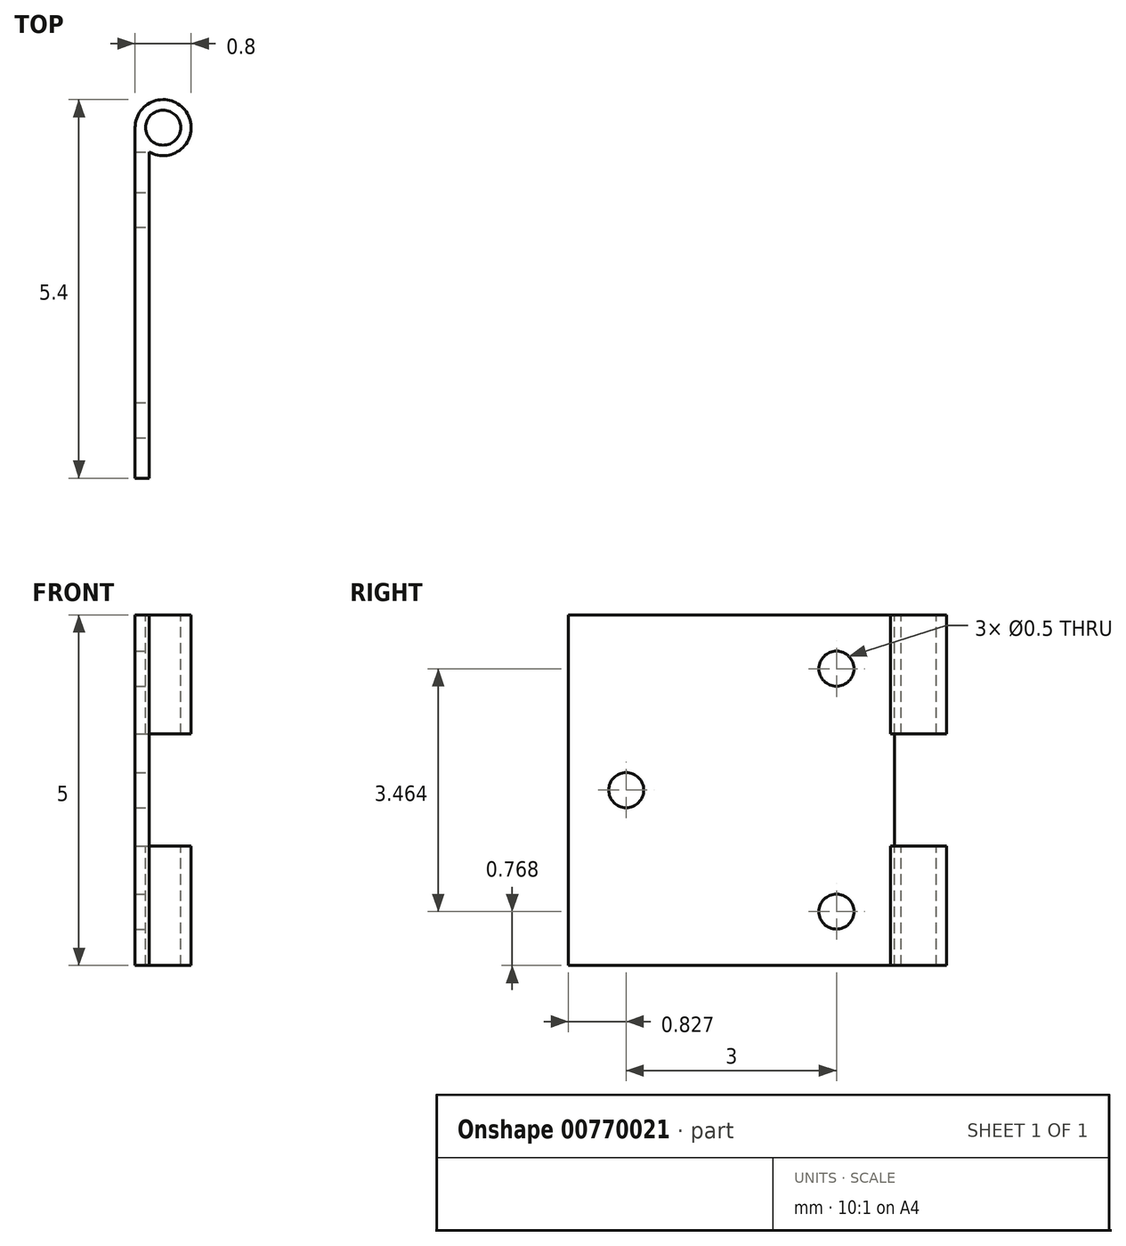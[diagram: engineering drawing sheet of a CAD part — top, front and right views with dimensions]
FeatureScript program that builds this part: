
annotation { "Feature Type Name" : "Feature", "Feature Type Description" : "" }
export const myFeature = defineFeature(function(context is Context, id is Id, definition is map)
    precondition{}
    {
        {
            var Q0;
            Q0=qCreatedBy(makeId("Front.planeOp"),FACE);
            var sketch = newSketch(context, id + "F0", { "sketchPlane" : qUnion([Q0])});
            skLineSegment(sketch, "E0", {"start": v(0, 0) * mm, "end": v(0, -5) * mm});
            skLineSegment(sketch, "E1", {"start": v(0, -5) * mm, "end": v(0.2, -5) * mm});
            skLineSegment(sketch, "E2", {"start": v(0.2, -5) * mm, "end": v(0.2, 0) * mm});
            skLineSegment(sketch, "E3", {"start": v(0.2, 0) * mm, "end": v(0, 0) * mm});
            skSolve(sketch);
        }
        {
            var Q0;
            Q0 = qSketchRegion(id + "F0", true);
            extrude(context, id + "F1", {"entities" : qUnion([Q0]), "oppositeDirection" : true, "depth" : 5 * mm, "offsetDistance" : 25 * mm});
        }
        {
            var Q0;
            Q0=makeQuery(id+"F1.opExtrude","SWEPT_FACE",FACE,{"disambiguationData":[OSD([sQuery(id+"F0.wireOp",EDGE,"E3")])]});
            var sketch = newSketch(context, id + "F2", { "sketchPlane" : qUnion([Q0])});
            skCircle(sketch, "E4", {"center": v(0.4, 5) * mm, "radius": 0.4 * mm});
            skSolve(sketch);
        }
        {
            var Q0;
            Q0 = qSketchRegion(id + "F2", true);
            extrude(context, id + "F3", {"entities" : qUnion([Q0]), "operationType" : NewBodyOperationType.ADD, "oppositeDirection" : true, "depth" : 5 * mm, "offsetDistance" : 25 * mm});
        }
        {
            var Q0;
            Q0=makeQuery(id+"F3.boolean.opBoolean","MERGE",FACE,{"derivedFrom":[makeQuery(id+"F1.opExtrude","SWEPT_FACE",FACE,{"disambiguationData":[OSD([sQuery(id+"F0.wireOp",EDGE,"E3")])]}),makeQuery(id+"F3.opExtrude","CAP_FACE",FACE,{"disambiguationData":[OSD([sQuery(id+"F2.wireOp",EDGE,"E4")])],"isStart":true})]});
            var sketch = newSketch(context, id + "F4", { "sketchPlane" : qUnion([Q0])});
            skCircle(sketch, "E5", {"center": v(0.4, 5) * mm, "radius": 0.25 * mm});
            skSolve(sketch);
        }
        {
            var Q0;
            Q0 = qSketchRegion(id + "F4", true);
            extrude(context, id + "F5", {"entities" : qUnion([Q0]), "operationType" : NewBodyOperationType.REMOVE, "endBound" : BoundingType.THROUGH_ALL, "oppositeDirection" : true, "depth" : 25 * mm, "offsetDistance" : 25 * mm});
        }
        {
            var Q0;
            Q0=makeQuery(id+"F1.opExtrude","CAP_FACE",FACE,{"disambiguationData":[OSD([sQuery(id+"F0.wireOp",EDGE,"E0"),sQuery(id+"F0.wireOp",EDGE,"E1"),sQuery(id+"F0.wireOp",EDGE,"E2"),sQuery(id+"F0.wireOp",EDGE,"E3")])],"isStart":true});
            var sketch = newSketch(context, id + "F6", { "sketchPlane" : qUnion([Q0])});
            skLineSegment(sketch, "E6", {"start": v(0.2, -2.5) * mm, "end": v(0.93, -2.5) * mm});
            skLineSegment(sketch, "E7", {"start": v(0.2, -2.5) * mm, "end": v(0.2, -1.7) * mm});
            skLineSegment(sketch, "E8", {"start": v(0.2, -2.5) * mm, "end": v(0.2, -3.3) * mm});
            skLineSegment(sketch, "E9", {"start": v(0.2, -1.7) * mm, "end": v(0.93, -1.7) * mm});
            skLineSegment(sketch, "E10", {"start": v(0.93, -1.7) * mm, "end": v(0.93, -2.5) * mm});
            skLineSegment(sketch, "E11", {"start": v(0.2, -3.3) * mm, "end": v(0.93, -3.3) * mm});
            skLineSegment(sketch, "E12", {"start": v(0.93, -3.3) * mm, "end": v(0.93, -2.5) * mm});
            skSolve(sketch);
        }
        {
            var Q0;
            Q0 = qSketchRegion(id + "F6", true);
            extrude(context, id + "F7", {"entities" : qUnion([Q0]), "operationType" : NewBodyOperationType.REMOVE, "endBound" : BoundingType.THROUGH_ALL, "oppositeDirection" : true, "depth" : 25 * mm, "offsetDistance" : 25 * mm});
        }
        {
            var Q0;
            Q0=makeQuery(id+"F7.boolean.opBoolean","MERGE",FACE,{"derivedFrom":[makeQuery(id+"F1.opExtrude","SWEPT_FACE",FACE,{"disambiguationData":[OSD([sQuery(id+"F0.wireOp",EDGE,"E2")])]}),makeQuery(id+"F7.opExtrude","SWEPT_FACE",FACE,{"disambiguationData":[OSD([sQuery(id+"F6.wireOp",EDGE,"E7"),sQuery(id+"F6.wireOp",EDGE,"E8")])]})]});
            var sketch = newSketch(context, id + "F8", { "sketchPlane" : qUnion([Q0])});
            skLineSegment(sketch, "E13", {"start": v(4.65, -1.7) * mm, "end": v(4.65, -3.3) * mm});
            skLineSegment(sketch, "E14", {"start": v(4.65, -3.3) * mm, "end": v(5.7, -3.3) * mm});
            skLineSegment(sketch, "E15", {"start": v(5.7, -3.3) * mm, "end": v(5.7, -1.7) * mm});
            skLineSegment(sketch, "E16", {"start": v(5.7, -1.7) * mm, "end": v(4.65, -1.7) * mm});
            skSolve(sketch);
        }
        {
            var Q0;
            Q0 = qSketchRegion(id + "F8", true);
            extrude(context, id + "F9", {"entities" : qUnion([Q0]), "operationType" : NewBodyOperationType.REMOVE, "endBound" : BoundingType.THROUGH_ALL, "oppositeDirection" : true, "depth" : 25 * mm, "offsetDistance" : 25 * mm});
        }
        {
            var Q0;
            Q0=makeQuery(id+"F7.boolean.opBoolean","MERGE",FACE,{"derivedFrom":[makeQuery(id+"F1.opExtrude","SWEPT_FACE",FACE,{"disambiguationData":[OSD([sQuery(id+"F0.wireOp",EDGE,"E2")])]}),makeQuery(id+"F7.opExtrude","SWEPT_FACE",FACE,{"disambiguationData":[OSD([sQuery(id+"F6.wireOp",EDGE,"E7"),sQuery(id+"F6.wireOp",EDGE,"E8")])]})]});
            var sketch = newSketch(context, id + "F10", { "sketchPlane" : qUnion([Q0])});
            skLineSegment(sketch, "E17", {"start": v(2.33, -2.5) * mm, "end": v(2.83, -2.5) * mm});
            skPoint(sketch, "E17.startSnap0", {"position": v(4.65, -2.5) * mm});
            skPoint(sketch, "E17.startSnap1", {"position": v(2.33, -5) * mm});
            skCircle(sketch, "E18.cCircle", {"center": v(2.83, -2.5) * mm, "radius": 1 * mm, "construction": true});
            skLineSegment(sketch, "E18.0", {"start": v(3.83, -0.77) * mm, "end": v(3.83, -4.23) * mm});
            skLineSegment(sketch, "E18.1", {"start": v(3.83, -4.23) * mm, "end": v(0.83, -2.5) * mm});
            skLineSegment(sketch, "E18.2", {"start": v(0.83, -2.5) * mm, "end": v(3.83, -0.77) * mm});
            skPoint(sketch, "E18.0.midPoint", {"position": v(3.83, -2.5) * mm});
            skCircle(sketch, "E19", {"center": v(3.83, -4.23) * mm, "radius": 0.25 * mm});
            skCircle(sketch, "E20", {"center": v(0.83, -2.5) * mm, "radius": 0.25 * mm});
            skCircle(sketch, "E21", {"center": v(3.83, -0.77) * mm, "radius": 0.25 * mm});
            skSolve(sketch);
        }
        {
            var Q0;
            {var subQ0=sQuery(id+"F10.wireOp",EDGE,"E18.2");var subQ1=sQuery(id+"F10.wireOp",EDGE,"E18.0");var subQ2=makeQuery(id+"F10.imprint","INTERSECT",VERTEX,{"derivedFrom":[subQ1,subQ0]});Q0=makeQuery(id+"F10.imprint","IMPRINT",FACE,{"disambiguationData":[TD([[makeQuery(id+"F10.imprint","IMPRINT",EDGE,{"disambiguationData":[TD([[subQ2,-1.0]])],"derivedFrom":subQ1}),-1.0]])]});}
            var Q1;
            {var subQ0=sQuery(id+"F10.wireOp",EDGE,"E18.2");var subQ1=sQuery(id+"F10.wireOp",EDGE,"E18.0");var subQ2=makeQuery(id+"F10.imprint","INTERSECT",VERTEX,{"derivedFrom":[subQ1,subQ0]});Q1=makeQuery(id+"F10.imprint","IMPRINT",FACE,{"disambiguationData":[TD([[makeQuery(id+"F10.imprint","IMPRINT",EDGE,{"disambiguationData":[TD([[subQ2,-1.0]])],"derivedFrom":subQ1}),1.0]])]});}
            var Q2;
            {var subQ0=sQuery(id+"F10.wireOp",EDGE,"E18.1");var subQ1=sQuery(id+"F10.wireOp",EDGE,"E18.0");var subQ2=makeQuery(id+"F10.imprint","INTERSECT",VERTEX,{"derivedFrom":[subQ1,subQ0]});Q2=makeQuery(id+"F10.imprint","IMPRINT",FACE,{"disambiguationData":[TD([[makeQuery(id+"F10.imprint","IMPRINT",EDGE,{"disambiguationData":[TD([[subQ2,1.0]])],"derivedFrom":subQ1}),-1.0]])]});}
            var Q3;
            {var subQ0=sQuery(id+"F10.wireOp",EDGE,"E18.1");var subQ1=sQuery(id+"F10.wireOp",EDGE,"E18.0");var subQ2=makeQuery(id+"F10.imprint","INTERSECT",VERTEX,{"derivedFrom":[subQ1,subQ0]});Q3=makeQuery(id+"F10.imprint","IMPRINT",FACE,{"disambiguationData":[TD([[makeQuery(id+"F10.imprint","IMPRINT",EDGE,{"disambiguationData":[TD([[subQ2,1.0]])],"derivedFrom":subQ1}),1.0]])]});}
            var Q4;
            {var subQ0=sQuery(id+"F10.wireOp",EDGE,"E18.2");var subQ1=sQuery(id+"F10.wireOp",EDGE,"E18.1");var subQ2=makeQuery(id+"F10.imprint","INTERSECT",VERTEX,{"derivedFrom":[subQ1,subQ0]});Q4=makeQuery(id+"F10.imprint","IMPRINT",FACE,{"disambiguationData":[TD([[makeQuery(id+"F10.imprint","IMPRINT",EDGE,{"disambiguationData":[TD([[subQ2,1.0]])],"derivedFrom":subQ1}),1.0]])]});}
            var Q5;
            {var subQ0=sQuery(id+"F10.wireOp",EDGE,"E18.2");var subQ1=sQuery(id+"F10.wireOp",EDGE,"E18.1");var subQ2=makeQuery(id+"F10.imprint","INTERSECT",VERTEX,{"derivedFrom":[subQ1,subQ0]});Q5=makeQuery(id+"F10.imprint","IMPRINT",FACE,{"disambiguationData":[TD([[makeQuery(id+"F10.imprint","IMPRINT",EDGE,{"disambiguationData":[TD([[subQ2,1.0]])],"derivedFrom":subQ1}),-1.0]])]});}
            extrude(context, id + "F11", {"entities" : qUnion([Q0, Q1, Q2, Q3, Q4, Q5]), "operationType" : NewBodyOperationType.REMOVE, "endBound" : BoundingType.THROUGH_ALL, "oppositeDirection" : true, "depth" : 25 * mm, "offsetDistance" : 25 * mm});
        }
    });
